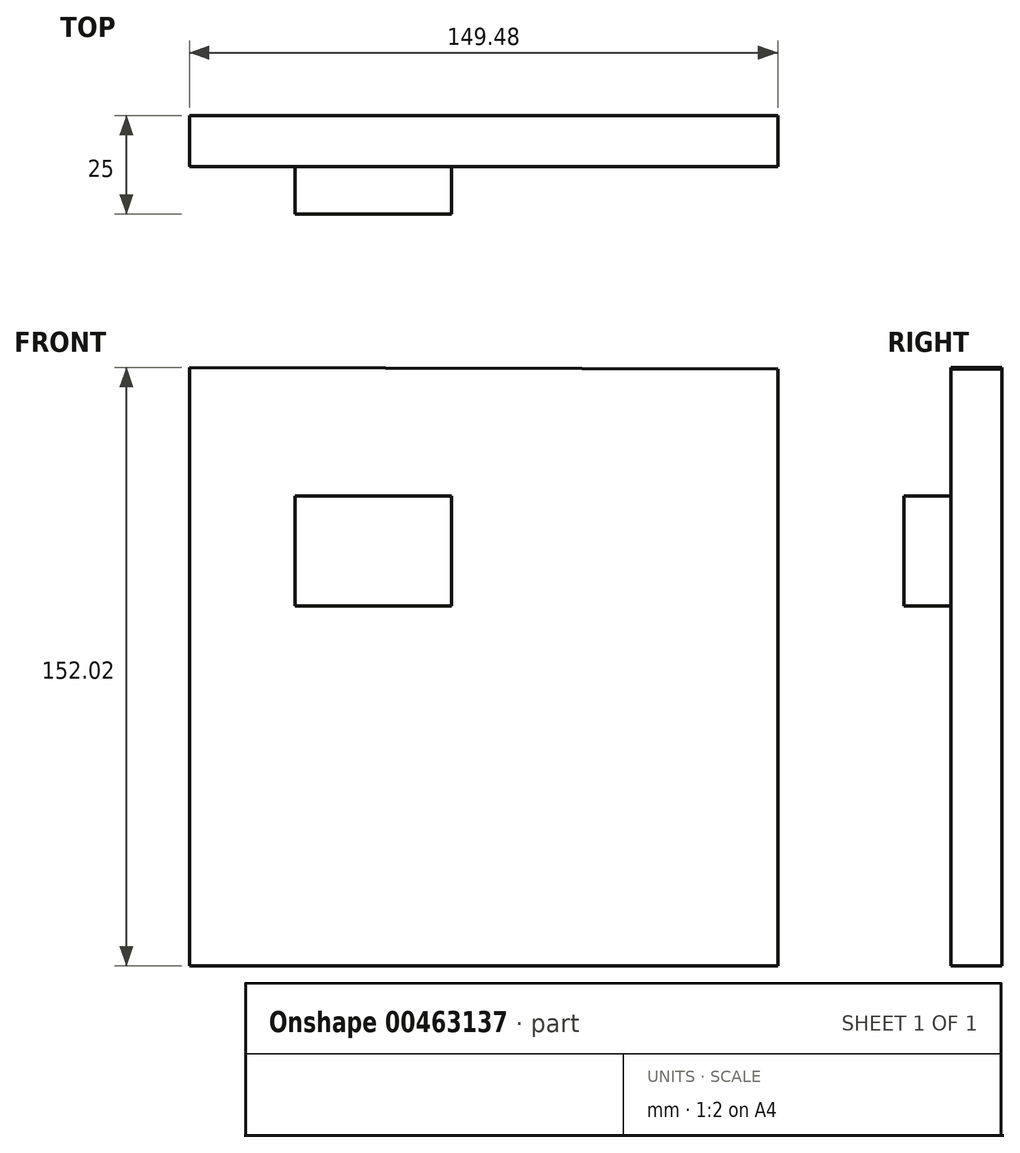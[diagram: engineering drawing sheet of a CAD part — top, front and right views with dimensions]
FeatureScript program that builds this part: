
annotation { "Feature Type Name" : "Feature", "Feature Type Description" : "" }
export const myFeature = defineFeature(function(context is Context, id is Id, definition is map)
    precondition{}
    {
        {
            var Q0;
            Q0=qCreatedBy(makeId("Front.planeOp"),FACE);
            var sketch = newSketch(context, id + "F0", { "sketchPlane" : qUnion([Q0])});
            skLineSegment(sketch, "E0", {"start": v(-74.26, 76.78) * mm, "end": v(-74.26, -75.24) * mm});
            skLineSegment(sketch, "E1", {"start": v(-74.26, -75.24) * mm, "end": v(75.22, -75.24) * mm});
            skLineSegment(sketch, "E2", {"start": v(75.22, -75.24) * mm, "end": v(75.22, 76.42) * mm});
            skLineSegment(sketch, "E3", {"start": v(75.22, 76.42) * mm, "end": v(-74.26, 76.78) * mm});
            skSolve(sketch);
        }
        {
            var Q0;
            Q0=makeQuery(id+"F0.imprint","IMPRINT",FACE,{"disambiguationData":[TD([[makeQuery(id+"F0.imprint","IMPRINT",EDGE,{"derivedFrom":sQuery(id+"F0.wireOp",EDGE,"E0")}),1.0]])]});
            extrude(context, id + "F1", {"entities" : qUnion([Q0]), "oppositeDirection" : true, "depth" : 13 * mm});
        }
        {
            var Q0;
            Q0=makeQuery(id+"F1.opExtrude","CAP_FACE",FACE,{"disambiguationData":[OSD([sQuery(id+"F0.wireOp",EDGE,"E0"),sQuery(id+"F0.wireOp",EDGE,"E1"),sQuery(id+"F0.wireOp",EDGE,"E2"),sQuery(id+"F0.wireOp",EDGE,"E3")])],"isStart":false});
            var sketch = newSketch(context, id + "F2", { "sketchPlane" : qUnion([Q0])});
            skSolve(sketch);
        }
        {
            var Q0;
            Q0=makeQuery(id+"F2.imprint","IMPRINT",FACE,{"disambiguationData":[TD([[makeQuery(id+"F2.imprint","IMPRINT",EDGE,{"derivedFrom":makeQuery(id+"F1.opExtrude","CAP_EDGE",EDGE,{"disambiguationData":[OSD([sQuery(id+"F0.wireOp",EDGE,"E0")])],"isStart":false})}),-1.0]])]});
            var sketch = newSketch(context, id + "F3", { "sketchPlane" : qUnion([Q0])});
            skLineSegment(sketch, "E4.bottom", {"start": v(-44.65, 43.9) * mm, "end": v(-5.12, 43.9) * mm});
            skLineSegment(sketch, "E4.top", {"start": v(-44.65, 13.28) * mm, "end": v(-5.12, 13.28) * mm});
            skLineSegment(sketch, "E4.left", {"start": v(-44.65, 43.9) * mm, "end": v(-44.65, 13.28) * mm});
            skLineSegment(sketch, "E4.right", {"start": v(-5.12, 43.9) * mm, "end": v(-5.12, 13.28) * mm});
            skPoint(sketch, "E4.middle", {"position": v(-24.89, 28.6) * mm});
            skLineSegment(sketch, "E5.bottom", {"start": v(7.64, 44.16) * mm, "end": v(47.35, 44.16) * mm});
            skLineSegment(sketch, "E5.top", {"start": v(7.64, 16.18) * mm, "end": v(47.35, 16.18) * mm});
            skLineSegment(sketch, "E5.left", {"start": v(7.64, 44.16) * mm, "end": v(7.64, 16.18) * mm});
            skLineSegment(sketch, "E5.right", {"start": v(47.35, 44.16) * mm, "end": v(47.35, 16.18) * mm});
            skPoint(sketch, "E5.middle", {"position": v(27.5, 30.17) * mm});
            skLineSegment(sketch, "E6.bottom", {"start": v(-44.79, -6.95) * mm, "end": v(-4.15, -6.95) * mm});
            skLineSegment(sketch, "E6.top", {"start": v(-44.79, -39.08) * mm, "end": v(-4.15, -39.08) * mm});
            skLineSegment(sketch, "E6.left", {"start": v(-44.79, -6.95) * mm, "end": v(-44.79, -39.08) * mm});
            skLineSegment(sketch, "E6.right", {"start": v(-4.15, -6.95) * mm, "end": v(-4.15, -39.08) * mm});
            skPoint(sketch, "E6.middle", {"position": v(-24.47, -23.02) * mm});
            skLineSegment(sketch, "E7.bottom", {"start": v(9.76, -4.12) * mm, "end": v(49.63, -4.12) * mm});
            skLineSegment(sketch, "E7.top", {"start": v(9.76, -43.72) * mm, "end": v(49.63, -43.72) * mm});
            skLineSegment(sketch, "E7.left", {"start": v(9.76, -4.12) * mm, "end": v(9.76, -43.72) * mm});
            skLineSegment(sketch, "E7.right", {"start": v(49.63, -4.12) * mm, "end": v(49.63, -43.72) * mm});
            skPoint(sketch, "E7.middle", {"position": v(29.7, -23.92) * mm});
            skSolve(sketch);
        }
        {
            var Q0;
            Q0=makeQuery(id+"F3.imprint","IMPRINT",FACE,{"disambiguationData":[TD([[makeQuery(id+"F3.imprint","IMPRINT",EDGE,{"derivedFrom":sQuery(id+"F3.wireOp",EDGE,"E4.bottom")}),-1.0]])]});
            var sketch = newSketch(context, id + "F4", { "sketchPlane" : qUnion([Q0])});
            skSolve(sketch);
        }
        {
            var Q0;
            Q0=makeQuery(id+"F4.imprint","IMPRINT",FACE,{"disambiguationData":[TD([[makeQuery(id+"F4.imprint","IMPRINT",EDGE,{"derivedFrom":makeQuery(id+"F3.imprint","IMPRINT",EDGE,{"derivedFrom":sQuery(id+"F3.wireOp",EDGE,"E4.bottom")})}),-1.0]])]});
            extrude(context, id + "F5", {"entities" : qUnion([Q0]), "operationType" : NewBodyOperationType.ADD, "oppositeDirection" : true, "depth" : 12 * mm});
        }
        {
            var Q0;
            Q0=makeQuery(id+"F3.imprint","IMPRINT",FACE,{"disambiguationData":[TD([[makeQuery(id+"F3.imprint","IMPRINT",EDGE,{"derivedFrom":sQuery(id+"F3.wireOp",EDGE,"E5.bottom")}),-1.0]])]});
            extrude(context, id + "F6", {"entities" : qUnion([Q0]), "operationType" : NewBodyOperationType.ADD, "oppositeDirection" : true, "depth" : 25 * mm});
        }
    });
